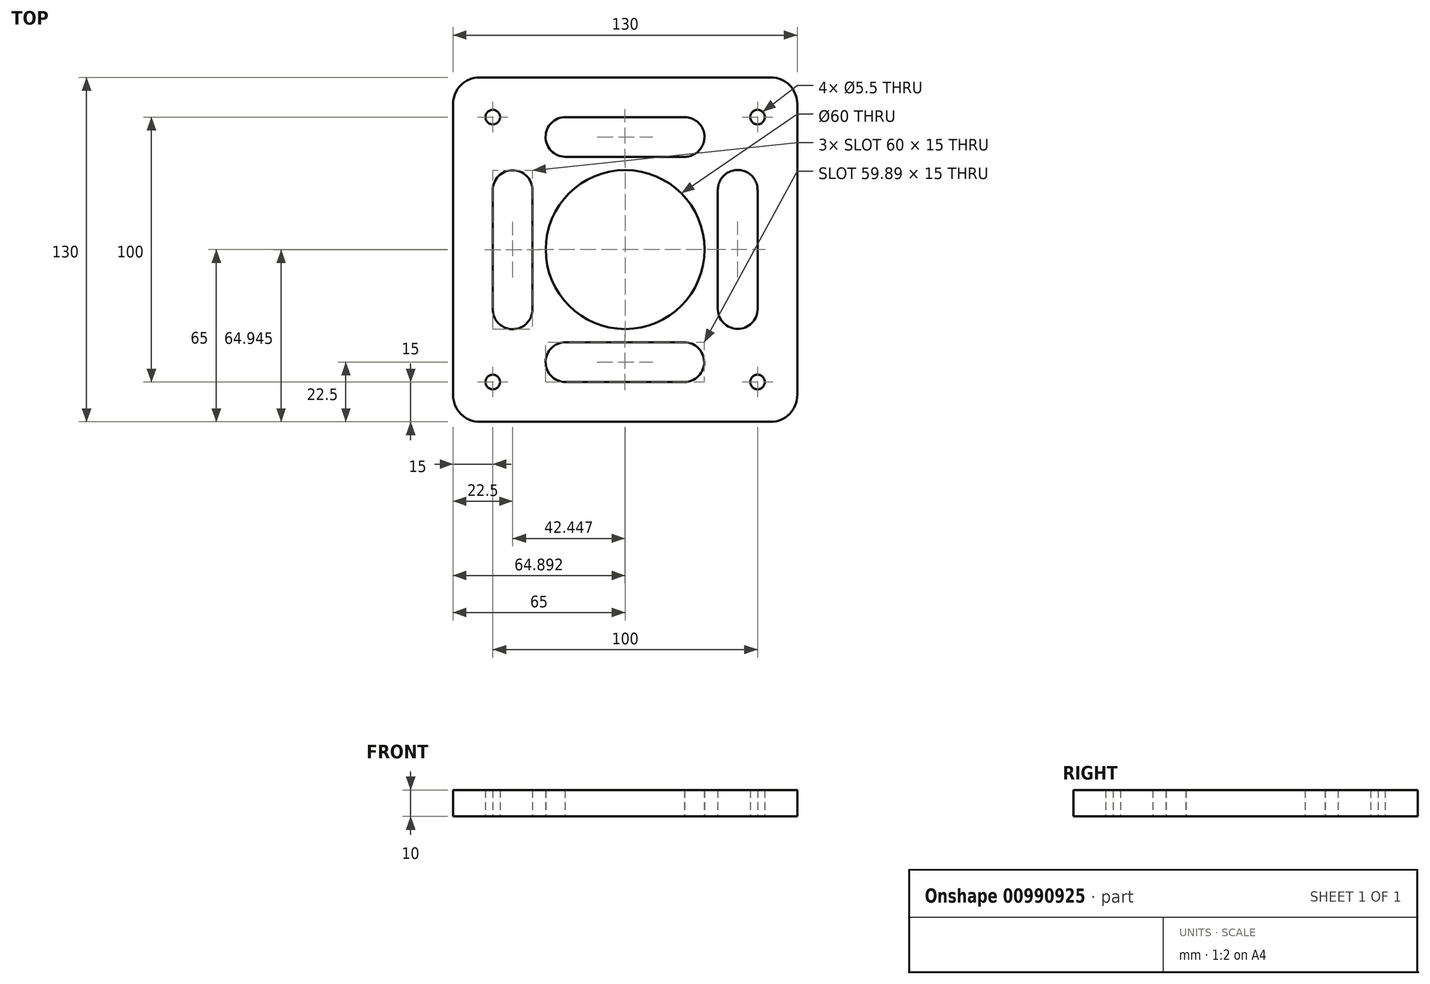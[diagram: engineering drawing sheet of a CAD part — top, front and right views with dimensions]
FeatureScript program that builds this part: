
annotation { "Feature Type Name" : "Feature", "Feature Type Description" : "" }
export const myFeature = defineFeature(function(context is Context, id is Id, definition is map)
    precondition{}
    {
        {
            var Q0;
            Q0=qCreatedBy(makeId("Top.planeOp"),FACE);
            var sketch = newSketch(context, id + "F0", { "sketchPlane" : qUnion([Q0])});
            skLineSegment(sketch, "E0.bottom", {"start": v(55, -65) * mm, "end": v(-55, -65) * mm});
            skLineSegment(sketch, "E0.top", {"start": v(55, 65) * mm, "end": v(-55, 65) * mm});
            skLineSegment(sketch, "E0.left", {"start": v(65, -55) * mm, "end": v(65, 55) * mm});
            skLineSegment(sketch, "E0.right", {"start": v(-65, -55) * mm, "end": v(-65, 55) * mm});
            skPoint(sketch, "E0.middle", {"position": v(0, 0) * mm});
            skCircle(sketch, "E1", {"center": v(0, 0) * mm, "radius": 30 * mm});
            skLineSegment(sketch, "E2", {"start": v(30, 0) * mm, "end": v(65, 0) * mm, "construction": true});
            skLineSegment(sketch, "E3", {"start": v(0, -30) * mm, "end": v(0, -65) * mm, "construction": true});
            skCircle(sketch, "E4", {"center": v(-50, 50) * mm, "radius": 2.75 * mm});
            skCircle(sketch, "E5.MirrorC", {"center": v(50, 50) * mm, "radius": 2.75 * mm});
            skCircle(sketch, "E6.MirrorC", {"center": v(-50, -50) * mm, "radius": 2.75 * mm});
            skCircle(sketch, "E7.MirrorC", {"center": v(50, -50) * mm, "radius": 2.75 * mm});
            skLineSegment(sketch, "E8", {"start": v(-50, 50) * mm, "end": v(-50, -50) * mm, "construction": true});
            skLineSegment(sketch, "E9", {"start": v(-50, -50) * mm, "end": v(50, -50) * mm, "construction": true});
            skLineSegment(sketch, "E10", {"start": v(50, -50) * mm, "end": v(50, 50) * mm, "construction": true});
            skLineSegment(sketch, "E11", {"start": v(50, 50) * mm, "end": v(-50, 50) * mm, "construction": true});
            skLineSegment(sketch, "E12.left", {"start": v(-35, -22.45) * mm, "end": v(-35, 22.55) * mm});
            skLineSegment(sketch, "E12.right", {"start": v(-50, -22.55) * mm, "end": v(-50, 22.45) * mm});
            skLineSegment(sketch, "E13.MirrorCS", {"start": v(50, -22.55) * mm, "end": v(50, 22.45) * mm});
            skLineSegment(sketch, "E14.MirrorCS", {"start": v(35, -22.45) * mm, "end": v(35, 22.55) * mm});
            skLineSegment(sketch, "E15.MirrorCS", {"start": v(22.34, -35) * mm, "end": v(-22.66, -35) * mm});
            skLineSegment(sketch, "E16.MirrorCS", {"start": v(22.45, -50) * mm, "end": v(-22.55, -50) * mm});
            skLineSegment(sketch, "E17.MirrorCS", {"start": v(22.34, 35) * mm, "end": v(-22.66, 35) * mm});
            skLineSegment(sketch, "E18.MirrorCS", {"start": v(22.45, 50) * mm, "end": v(-22.55, 50) * mm});
            skArc(sketch, "E19", {"start": v(-35, 22.55) * mm, "mid": v(-42.55, 29.95) * mm, "end": v(-50, 22.45) * mm});
            skArc(sketch, "E20", {"start": v(-50, -22.55) * mm, "mid": v(-42.44, -30.06) * mm, "end": v(-35, -22.45) * mm});
            skArc(sketch, "E21", {"start": v(-22.66, -35) * mm, "mid": v(-30.05, -42.55) * mm, "end": v(-22.55, -50) * mm});
            skArc(sketch, "E22", {"start": v(22.45, -50) * mm, "mid": v(29.84, -42.45) * mm, "end": v(22.34, -35) * mm});
            skArc(sketch, "E23", {"start": v(35, -22.45) * mm, "mid": v(42.45, -29.95) * mm, "end": v(50, -22.55) * mm});
            skArc(sketch, "E24", {"start": v(50, 22.45) * mm, "mid": v(42.56, 30.06) * mm, "end": v(35, 22.55) * mm});
            skArc(sketch, "E25", {"start": v(22.34, 35) * mm, "mid": v(29.95, 42.44) * mm, "end": v(22.45, 50) * mm});
            skArc(sketch, "E26", {"start": v(-22.55, 50) * mm, "mid": v(-30.05, 42.55) * mm, "end": v(-22.66, 35) * mm});
            skPoint(sketch, "E27.visualSharp", {"position": v(-65, 65) * mm});
            skArc(sketch, "E27.filletArc", {"start": v(-55, 65) * mm, "mid": v(-62.07, 62.07) * mm, "end": v(-65, 55) * mm});
            skPoint(sketch, "E28.visualSharp", {"position": v(65, 65) * mm});
            skArc(sketch, "E28.filletArc", {"start": v(65, 55) * mm, "mid": v(62.07, 62.07) * mm, "end": v(55, 65) * mm});
            skPoint(sketch, "E29.visualSharp", {"position": v(65, -65) * mm});
            skArc(sketch, "E29.filletArc", {"start": v(55, -65) * mm, "mid": v(62.07, -62.07) * mm, "end": v(65, -55) * mm});
            skPoint(sketch, "E30.visualSharp", {"position": v(-65, -65) * mm});
            skArc(sketch, "E30.filletArc", {"start": v(-65, -55) * mm, "mid": v(-62.07, -62.07) * mm, "end": v(-55, -65) * mm});
            skSolve(sketch);
        }
        {
            var Q0;
            Q0 = qSketchRegion(id + "F0", true);
            extrude(context, id + "F1", {"entities" : qUnion([Q0]), "depth" : 10 * mm, "offsetDistance" : 25 * mm});
        }
    });
